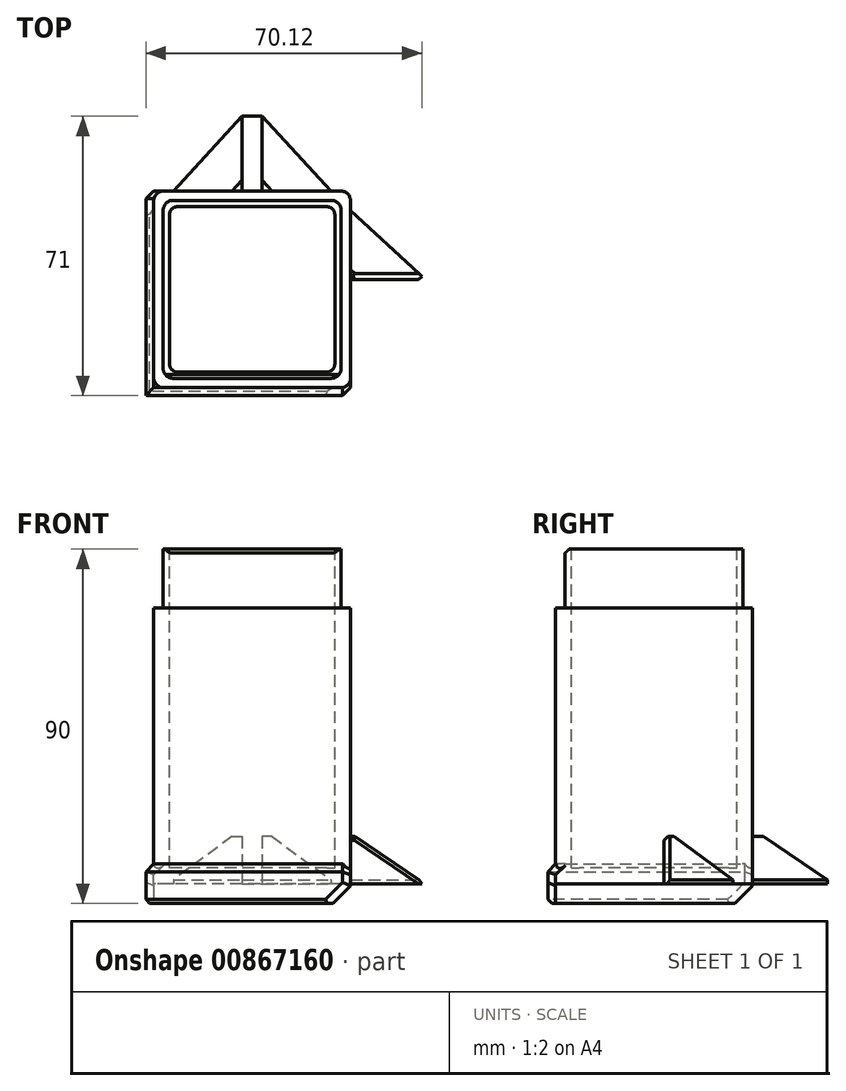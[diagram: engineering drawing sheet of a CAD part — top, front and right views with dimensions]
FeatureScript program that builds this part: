
annotation { "Feature Type Name" : "Feature", "Feature Type Description" : "" }
export const myFeature = defineFeature(function(context is Context, id is Id, definition is map)
    precondition{}
    {
        {
            var Q0;
            Q0=qCreatedBy(makeId("Top.planeOp"),FACE);
            var sketch = newSketch(context, id + "F0", { "sketchPlane" : qUnion([Q0])});
            skLineSegment(sketch, "E0.bottom", {"start": v(25, 25) * mm, "end": v(-25, 25) * mm});
            skLineSegment(sketch, "E0.top", {"start": v(25, -25) * mm, "end": v(-25, -25) * mm});
            skLineSegment(sketch, "E0.left", {"start": v(25, 25) * mm, "end": v(25, -25) * mm});
            skLineSegment(sketch, "E0.right", {"start": v(-25, 25) * mm, "end": v(-25, -25) * mm});
            skPoint(sketch, "E0.middle", {"position": v(0, 0) * mm});
            skSolve(sketch);
        }
        {
            var Q0;
            Q0=qSketchRegion(id+"F0",true);
            extrude(context, id + "F1", {"entities" : qUnion([Q0]), "depth" : 70 * mm, "offsetDistance" : 25 * mm});
        }
        {
            var Q0;
            Q0=makeQuery(id+"F1.opExtrude","CAP_FACE",FACE,{"disambiguationData":[OSD([sQuery(id+"F0.wireOp",EDGE,"E0.bottom"),sQuery(id+"F0.wireOp",EDGE,"E0.top"),sQuery(id+"F0.wireOp",EDGE,"E0.left"),sQuery(id+"F0.wireOp",EDGE,"E0.right")])],"isStart":false});
            var sketch = newSketch(context, id + "F2", { "sketchPlane" : qUnion([Q0])});
            skLineSegment(sketch, "E1.bottom", {"start": v(22.6, 22.6) * mm, "end": v(-22.6, 22.6) * mm});
            skLineSegment(sketch, "E1.top", {"start": v(22.6, -22.6) * mm, "end": v(-22.6, -22.6) * mm});
            skLineSegment(sketch, "E1.left", {"start": v(22.6, 22.6) * mm, "end": v(22.6, -22.6) * mm});
            skLineSegment(sketch, "E1.right", {"start": v(-22.6, 22.6) * mm, "end": v(-22.6, -22.6) * mm});
            skPoint(sketch, "E1.middle", {"position": v(0, 0) * mm});
            skSolve(sketch);
        }
        {
            var Q0;
            Q0=qSketchRegion(id+"F2",true);
            extrude(context, id + "F3", {"entities" : qUnion([Q0]), "operationType" : NewBodyOperationType.ADD, "depth" : 15 * mm, "offsetDistance" : 25 * mm});
        }
        {
            var Q0;
            Q0=makeQuery(id+"F2.imprint","IMPRINT",FACE,{"disambiguationData":[TD([[makeQuery(id+"F2.imprint","IMPRINT",EDGE,{"derivedFrom":sQuery(id+"F2.wireOp",EDGE,"E1.bottom")}),-1.0]])]});
            var sketch = newSketch(context, id + "F4", { "sketchPlane" : qUnion([Q0])});
            skLineSegment(sketch, "E2.bottom", {"start": v(21, 21) * mm, "end": v(-21, 21) * mm});
            skLineSegment(sketch, "E2.top", {"start": v(21, -21) * mm, "end": v(-21, -21) * mm});
            skLineSegment(sketch, "E2.left", {"start": v(21, 21) * mm, "end": v(21, -21) * mm});
            skLineSegment(sketch, "E2.right", {"start": v(-21, 21) * mm, "end": v(-21, -21) * mm});
            skPoint(sketch, "E2.middle", {"position": v(0, 0) * mm});
            skSolve(sketch);
        }
        {
            var Q0;
            Q0=qSketchRegion(id+"F4",true);
            extrude(context, id + "F5", {"entities" : qUnion([Q0]), "operationType" : NewBodyOperationType.REMOVE, "oppositeDirection" : true, "depth" : 66 * mm, "offsetDistance" : 25 * mm, "hasSecondDirection" : true, "secondDirectionBound" : SecondDirectionBoundingType.UP_TO_NEXT, "secondDirectionOppositeDirection" : false, "secondDirectionDepth" : 25 * mm});
        }
        {
            var Q0;
            Q0=makeQuery(id+"F5.boolean.opBoolean","COPY",EDGE,{"derivedFrom":makeQuery(id+"F5.opExtrude","SWEPT_EDGE",EDGE,{"disambiguationData":[OSD([sQuery(id+"F4.wireOp",EDGE,"E2.top"),sQuery(id+"F4.wireOp",EDGE,"E2.right")])]})});
            var Q1;
            Q1=makeQuery(id+"F5.boolean.opBoolean","COPY",EDGE,{"derivedFrom":makeQuery(id+"F5.opExtrude","SWEPT_EDGE",EDGE,{"disambiguationData":[OSD([sQuery(id+"F4.wireOp",EDGE,"E2.bottom"),sQuery(id+"F4.wireOp",EDGE,"E2.right")])]})});
            var Q2;
            Q2=makeQuery(id+"F5.boolean.opBoolean","COPY",EDGE,{"derivedFrom":makeQuery(id+"F5.opExtrude","SWEPT_EDGE",EDGE,{"disambiguationData":[OSD([sQuery(id+"F4.wireOp",EDGE,"E2.bottom"),sQuery(id+"F4.wireOp",EDGE,"E2.left")])]})});
            var Q3;
            Q3=makeQuery(id+"F5.boolean.opBoolean","COPY",EDGE,{"derivedFrom":makeQuery(id+"F5.opExtrude","SWEPT_EDGE",EDGE,{"disambiguationData":[OSD([sQuery(id+"F4.wireOp",EDGE,"E2.top"),sQuery(id+"F4.wireOp",EDGE,"E2.left")])]})});
            fillet(context, id + "F6", {"entities" : qUnion([Q0, Q1, Q2, Q3]), "radius" : 2 * mm, "tangentPropagation" : true, "allowEdgeOverflow" : false});
        }
        {
            var Q0;
            Q0=makeQuery(id+"F3.opExtrude","CAP_EDGE",EDGE,{"disambiguationData":[OSD([sQuery(id+"F2.wireOp",EDGE,"E1.top")])],"isStart":false});
            chamfer(context, id + "F7", {"entities" : qUnion([Q0]), "width" : 1 * mm, "tangentPropagation" : true});
        }
        {
            var Q0;
            Q0=qCreatedBy(makeId("Top.planeOp"),FACE);
            cPlane(context, id + "F8", {"entities" : qUnion([Q0]), "cplaneType" : CPlaneType.OFFSET, "offset" : 1 * mm, "width" : 150 * mm, "height" : 150 * mm});
        }
        {
            var Q0;
            Q0=qCreatedBy(makeId("Top.planeOp"),FACE);
            var sketch = newSketch(context, id + "F9", { "sketchPlane" : qUnion([Q0])});
            skLineSegment(sketch, "E3", {"start": v(25, 20) * mm, "end": v(25, -2.5) * mm});
            skPoint(sketch, "E4", {"position": v(25, 0) * mm});
            skLineSegment(sketch, "E5", {"start": v(44, 2.5) * mm, "end": v(25, 20) * mm});
            skPoint(sketch, "E6", {"position": v(44, 2.5) * mm});
            skPoint(sketch, "E7", {"position": v(44, -2.5) * mm});
            skLineSegment(sketch, "E8", {"start": v(44, 2.5) * mm, "end": v(44, -2.5) * mm});
            skLineSegment(sketch, "E9", {"start": v(44, -2.5) * mm, "end": v(25, -2.5) * mm});
            skSolve(sketch);
        }
        {
            var Q0;
            Q0=qSketchRegion(id+"F9",true);
            extrude(context, id + "F10", {"entities" : qUnion([Q0]), "operationType" : NewBodyOperationType.ADD, "depth" : 12 * mm, "offsetDistance" : 25 * mm});
        }
        {
            var Q0;
            Q0=makeQuery(id+"F10.opExtrude","CAP_EDGE",EDGE,{"disambiguationData":[OSD([sQuery(id+"F9.wireOp",EDGE,"E5")])],"isStart":false});
            var Q1;
            Q1=makeQuery(id+"F10.opExtrude","CAP_EDGE",EDGE,{"disambiguationData":[OSD([sQuery(id+"F9.wireOp",EDGE,"UztwefAy-fSHT-pq0R-qJ08-BBRRVytWD2CF")])],"isStart":false});
            chamfer(context, id + "F11", {"entities" : qUnion([Q0, Q1]), "width" : 11 * mm, "tangentPropagation" : true});
        }
        {
            var Q0;
            Q0=qCreatedBy(makeId("Top.planeOp"),FACE);
            var sketch = newSketch(context, id + "F12", { "sketchPlane" : qUnion([Q0])});
            skLineSegment(sketch, "E10.bottom", {"start": v(25, 2.5) * mm, "end": v(45, 2.5) * mm});
            skLineSegment(sketch, "E10.top", {"start": v(25, -2.5) * mm, "end": v(45, -2.5) * mm});
            skLineSegment(sketch, "E10.left", {"start": v(25, 2.5) * mm, "end": v(25, -2.5) * mm});
            skLineSegment(sketch, "E10.right", {"start": v(45, 2.5) * mm, "end": v(45, -2.5) * mm});
            skPoint(sketch, "E11", {"position": v(25, 0) * mm});
            skSolve(sketch);
        }
        {
            var Q0;
            Q0=qSketchRegion(id+"F12",true);
            extrude(context, id + "F13", {"entities" : qUnion([Q0]), "operationType" : NewBodyOperationType.REMOVE, "depth" : 20 * mm, "offsetDistance" : 25 * mm});
        }
        {
            var Q0;
            Q0=qCreatedBy(makeId("Top.planeOp"),FACE);
            var sketch = newSketch(context, id + "F14", { "sketchPlane" : qUnion([Q0])});
            skLineSegment(sketch, "E12", {"start": v(-20, 25) * mm, "end": v(20, 25) * mm});
            skLineSegment(sketch, "E13", {"start": v(-2.5, 44) * mm, "end": v(-20, 25) * mm});
            skLineSegment(sketch, "E14", {"start": v(2.5, 44) * mm, "end": v(20, 25) * mm});
            skLineSegment(sketch, "E15", {"start": v(-2.5, 44) * mm, "end": v(2.5, 44) * mm});
            skPoint(sketch, "E16", {"position": v(0, 44) * mm});
            skSolve(sketch);
        }
        {
            var Q0;
            Q0=qSketchRegion(id+"F14",true);
            extrude(context, id + "F15", {"entities" : qUnion([Q0]), "operationType" : NewBodyOperationType.ADD, "depth" : 12 * mm, "offsetDistance" : 25 * mm});
        }
        {
            var Q0;
            Q0=makeQuery(id+"F15.opExtrude","CAP_EDGE",EDGE,{"disambiguationData":[OSD([sQuery(id+"F14.wireOp",EDGE,"E13")])],"isStart":false});
            var Q1;
            Q1=makeQuery(id+"F15.opExtrude","CAP_EDGE",EDGE,{"disambiguationData":[OSD([sQuery(id+"F14.wireOp",EDGE,"E14")])],"isStart":false});
            chamfer(context, id + "F16", {"entities" : qUnion([Q0, Q1]), "width" : 11 * mm, "tangentPropagation" : true});
        }
        {
            var Q0;
            Q0=qCreatedBy(id+"F8.planeOp",FACE);
            var sketch = newSketch(context, id + "F17", { "sketchPlane" : qUnion([Q0])});
            skLineSegment(sketch, "E17.bottom", {"start": v(-2.5, 25) * mm, "end": v(-2.5, 45) * mm});
            skLineSegment(sketch, "E17.top", {"start": v(2.5, 25) * mm, "end": v(2.5, 45) * mm});
            skLineSegment(sketch, "E17.left", {"start": v(-2.5, 25) * mm, "end": v(2.5, 25) * mm});
            skLineSegment(sketch, "E17.right", {"start": v(-2.5, 45) * mm, "end": v(2.5, 45) * mm});
            skPoint(sketch, "E18", {"position": v(0, 25) * mm});
            skSolve(sketch);
        }
        {
            var Q0;
            Q0=qSketchRegion(id+"F17",true);
            extrude(context, id + "F18", {"entities" : qUnion([Q0]), "operationType" : NewBodyOperationType.REMOVE, "depth" : 20 * mm, "offsetDistance" : 25 * mm});
        }
        {
            var Q0;
            Q0=makeQuery(id+"F13.boolean.opBoolean","INTERSECT",EDGE,{"derivedFrom":[makeQuery(id+"F11.opChamfer","BLEND_FACE",FACE,{"disambiguationData":[OSD([sQuery(id+"F9.wireOp",EDGE,"E5")])]}),makeQuery(id+"F13.opExtrude","SWEPT_FACE",FACE,{"disambiguationData":[OSD([sQuery(id+"F12.wireOp",EDGE,"E10.bottom")])]})]});
            var Q1;
            Q1=makeQuery(id+"F13.boolean.opBoolean","INTERSECT",EDGE,{"derivedFrom":[makeQuery(id+"F10.opExtrude","CAP_FACE",FACE,{"disambiguationData":[OSD([sQuery(id+"F9.wireOp",EDGE,"E3"),sQuery(id+"F9.wireOp",EDGE,"E5"),sQuery(id+"F9.wireOp",EDGE,"E8"),sQuery(id+"F9.wireOp",EDGE,"E9")])],"isStart":false}),makeQuery(id+"F13.opExtrude","SWEPT_FACE",FACE,{"disambiguationData":[OSD([sQuery(id+"F12.wireOp",EDGE,"E10.bottom")])]})]});
            chamfer(context, id + "F19", {"entities" : qUnion([Q0, Q1]), "width" : 1 * mm, "tangentPropagation" : true});
        }
        {
            var Q0;
            Q0=qCreatedBy(makeId("Top.planeOp"),FACE);
            var sketch = newSketch(context, id + "F20", { "sketchPlane" : qUnion([Q0])});
            skLineSegment(sketch, "E19", {"start": v(-27, 25) * mm, "end": v(-27, -27) * mm});
            skLineSegment(sketch, "E20", {"start": v(-27, -27) * mm, "end": v(25, -27) * mm});
            skLineSegment(sketch, "E21", {"start": v(25, -27) * mm, "end": v(25, -25) * mm});
            skLineSegment(sketch, "E22", {"start": v(25, -25) * mm, "end": v(-25, -25) * mm});
            skLineSegment(sketch, "E23", {"start": v(-25, -25) * mm, "end": v(-25, 25) * mm});
            skLineSegment(sketch, "E24", {"start": v(-25, 25) * mm, "end": v(-27, 25) * mm});
            skSolve(sketch);
        }
        {
            var Q0;
            Q0 = qSketchRegion(id + "F20", true);
            extrude(context, id + "F21", {"entities" : qUnion([Q0]), "operationType" : NewBodyOperationType.ADD, "endBound" : BoundingType.SYMMETRIC, "depth" : 10 * mm, "offsetDistance" : 25 * mm});
        }
        {
            var Q0;
            Q0=makeQuery(id+"F1.opExtrude","SWEPT_EDGE",EDGE,{"disambiguationData":[OSD([sQuery(id+"F0.wireOp",EDGE,"E0.bottom"),sQuery(id+"F0.wireOp",EDGE,"E0.left")])]});
            var Q1;
            Q1=makeQuery(id+"F3.opExtrude","SWEPT_EDGE",EDGE,{"disambiguationData":[OSD([sQuery(id+"F2.wireOp",EDGE,"E1.bottom"),sQuery(id+"F2.wireOp",EDGE,"E1.right")])]});
            var Q2;
            Q2=makeQuery(id+"F1.opExtrude","SWEPT_EDGE",EDGE,{"disambiguationData":[OSD([sQuery(id+"F0.wireOp",EDGE,"E0.bottom"),sQuery(id+"F0.wireOp",EDGE,"E0.right")])]});
            var Q3;
            Q3=makeQuery(id+"F3.opExtrude","SWEPT_EDGE",EDGE,{"disambiguationData":[OSD([sQuery(id+"F2.wireOp",EDGE,"E1.bottom"),sQuery(id+"F2.wireOp",EDGE,"E1.left")])]});
            var Q4;
            Q4=makeQuery(id+"F3.opExtrude","SWEPT_EDGE",EDGE,{"disambiguationData":[OSD([sQuery(id+"F2.wireOp",EDGE,"E1.top"),sQuery(id+"F2.wireOp",EDGE,"E1.left")])]});
            var Q5;
            Q5=makeQuery(id+"F1.opExtrude","SWEPT_EDGE",EDGE,{"disambiguationData":[OSD([sQuery(id+"F0.wireOp",EDGE,"E0.top"),sQuery(id+"F0.wireOp",EDGE,"E0.left")])]});
            var Q6;
            Q6=makeQuery(id+"F3.opExtrude","SWEPT_EDGE",EDGE,{"disambiguationData":[OSD([sQuery(id+"F2.wireOp",EDGE,"E1.top"),sQuery(id+"F2.wireOp",EDGE,"E1.right")])]});
            var Q7;
            Q7=makeQuery(id+"F1.opExtrude","SWEPT_EDGE",EDGE,{"disambiguationData":[OSD([sQuery(id+"F0.wireOp",EDGE,"E0.top"),sQuery(id+"F0.wireOp",EDGE,"E0.right")])]});
            fillet(context, id + "F22", {"entities" : qUnion([Q0, Q1, Q2, Q3, Q4, Q5, Q6, Q7]), "radius" : 2.5 * mm, "tangentPropagation" : true, "allowEdgeOverflow" : false});
        }
        {
            var Q0;
            Q0=makeQuery(id+"F21.opExtrude","CAP_EDGE",EDGE,{"disambiguationData":[OSD([sQuery(id+"F20.wireOp",EDGE,"E19")])],"isStart":false});
            var Q1;
            Q1=makeQuery(id+"F21.opExtrude","CAP_EDGE",EDGE,{"disambiguationData":[OSD([sQuery(id+"F20.wireOp",EDGE,"E20")])],"isStart":false});
            chamfer(context, id + "F23", {"entities" : qUnion([Q0, Q1]), "width" : 2 * mm, "tangentPropagation" : true});
        }
        {
            var Q0;
            Q0=makeQuery(id+"F21.opExtrude","CAP_EDGE",EDGE,{"disambiguationData":[OSD([sQuery(id+"F20.wireOp",EDGE,"E24")])],"isStart":true});
            var Q1;
            Q1=makeQuery(id+"F21.opExtrude","CAP_EDGE",EDGE,{"disambiguationData":[OSD([sQuery(id+"F20.wireOp",EDGE,"E21")])],"isStart":true});
            chamfer(context, id + "F24", {"entities" : qUnion([Q0, Q1]), "width" : 4.5 * mm, "tangentPropagation" : true});
        }
        {
            var Q0;
            Q0=makeQuery(id+"F23.opChamfer","BLEND_EDGE",EDGE,{"blendedFrom":[makeQuery(id+"F21.opExtrude","CAP_EDGE",EDGE,{"disambiguationData":[OSD([sQuery(id+"F20.wireOp",EDGE,"E19")])],"isStart":false}),makeQuery(id+"F21.opExtrude","SWEPT_FACE",FACE,{"disambiguationData":[OSD([sQuery(id+"F20.wireOp",EDGE,"E24")])]})],"blendedInto":[makeQuery(id+"F21.opExtrude","SWEPT_FACE",FACE,{"disambiguationData":[OSD([sQuery(id+"F20.wireOp",EDGE,"E24")])]})]});
            var Q1;
            Q1=makeQuery(id+"F21.opExtrude","SWEPT_EDGE",EDGE,{"disambiguationData":[OSD([sQuery(id+"F20.wireOp",EDGE,"E19"),sQuery(id+"F20.wireOp",EDGE,"E24")])]});
            var Q2;
            Q2=makeQuery(id+"F24.opChamfer","BLEND_EDGE",EDGE,{"blendedFrom":[makeQuery(id+"F21.opExtrude","CAP_EDGE",EDGE,{"disambiguationData":[OSD([sQuery(id+"F20.wireOp",EDGE,"E24")])],"isStart":true}),makeQuery(id+"F21.opExtrude","SWEPT_FACE",FACE,{"disambiguationData":[OSD([sQuery(id+"F20.wireOp",EDGE,"E19")])]})],"blendedInto":[makeQuery(id+"F21.opExtrude","SWEPT_FACE",FACE,{"disambiguationData":[OSD([sQuery(id+"F20.wireOp",EDGE,"E19")])]})]});
            var Q3;
            Q3=makeQuery(id+"F23.opChamfer","BLEND_EDGE",EDGE,{"blendedFrom":[makeQuery(id+"F21.opExtrude","CAP_EDGE",EDGE,{"disambiguationData":[OSD([sQuery(id+"F20.wireOp",EDGE,"E20")])],"isStart":false}),makeQuery(id+"F21.opExtrude","SWEPT_FACE",FACE,{"disambiguationData":[OSD([sQuery(id+"F20.wireOp",EDGE,"E21")])]})],"blendedInto":[makeQuery(id+"F21.opExtrude","SWEPT_FACE",FACE,{"disambiguationData":[OSD([sQuery(id+"F20.wireOp",EDGE,"E21")])]})]});
            var Q4;
            Q4=makeQuery(id+"F21.opExtrude","SWEPT_EDGE",EDGE,{"disambiguationData":[OSD([sQuery(id+"F20.wireOp",EDGE,"E20"),sQuery(id+"F20.wireOp",EDGE,"E21")])]});
            var Q5;
            Q5=makeQuery(id+"F24.opChamfer","BLEND_EDGE",EDGE,{"blendedFrom":[makeQuery(id+"F21.opExtrude","CAP_EDGE",EDGE,{"disambiguationData":[OSD([sQuery(id+"F20.wireOp",EDGE,"E21")])],"isStart":true}),makeQuery(id+"F21.opExtrude","SWEPT_FACE",FACE,{"disambiguationData":[OSD([sQuery(id+"F20.wireOp",EDGE,"E20")])]})],"blendedInto":[makeQuery(id+"F21.opExtrude","SWEPT_FACE",FACE,{"disambiguationData":[OSD([sQuery(id+"F20.wireOp",EDGE,"E20")])]})]});
            chamfer(context, id + "F25", {"entities" : qUnion([Q0, Q1, Q2, Q3, Q4, Q5]), "width" : 2 * mm, "tangentPropagation" : true});
        }
        {
            var Q0;
            Q0=makeQuery(id+"F21.opExtrude","CAP_EDGE",EDGE,{"disambiguationData":[OSD([sQuery(id+"F20.wireOp",EDGE,"E19")])],"isStart":true});
            var Q1;
            Q1=makeQuery(id+"F21.opExtrude","CAP_EDGE",EDGE,{"disambiguationData":[OSD([sQuery(id+"F20.wireOp",EDGE,"E20")])],"isStart":true});
            chamfer(context, id + "F26", {"entities" : qUnion([Q0, Q1]), "width" : 1 * mm, "tangentPropagation" : true});
        }
    });
